# Revit family: 696-T2001_R TMV_OxBox
name_source: partatom
category: Plumbing Fixtures
units: mm (PartAtom-declared; Revit-internal decimal feet)

## family parameters
Always vertical = No
Cut with Voids When Loaded = Yes
Part Type = Normal
Room Calculation Point = No
Round Connector Dimension = Use Diameter
Shared = No
Work Plane-Based = Yes

## types (4) — shared parameters
Description = Thermostatic Mixing Valve with Ox Box
Manufacturer = Sioux Chief Manufacturing
Outlet Connector Type = MIXING VALVE WITH 3/8" COMPRESSION "MIX" AND COLD-BYPASS OUTLETS
URL = www.siouxchief.com
Vent Connection = No
Waste Connection = No
zero-valued in all types: Default Elevation

## per-type parameters (varying)
| type | Inlet Connector Type | Model |
| 696-T2001CR - 1/2" CPVC MALE | 1/2" CPVC MALE | 696-T2001CR |
| 696-T2001PR - 1/2" MSWT/PRESS/PUSH | 1/2" MSWT/PRESS/PUSH | 696-T2001PR |
| 696-T2001WR - F1960 PEX | 1/2" F1960 PEX CONNECTION | 696-T2001WR |
| 696-T2001XR - F1807 PEX | 1/2" F1807 PEX CONNECTION | 696-T2001XR |

## geometry (parser evidence)
native form markers: Sweep x3
no freeform markers — native parametric forms only
